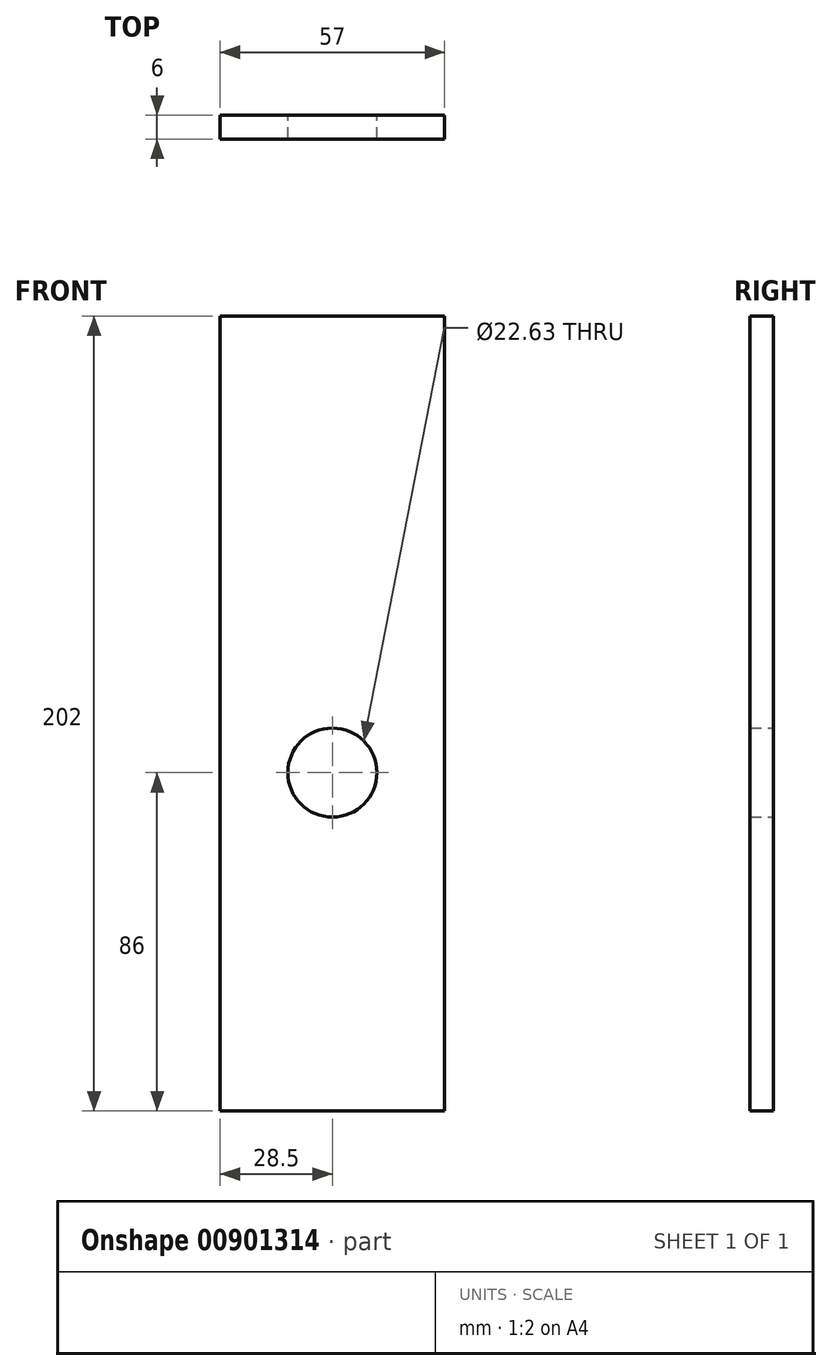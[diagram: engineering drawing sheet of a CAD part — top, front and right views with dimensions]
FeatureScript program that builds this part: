
annotation { "Feature Type Name" : "Feature", "Feature Type Description" : "" }
export const myFeature = defineFeature(function(context is Context, id is Id, definition is map)
    precondition{}
    {
        {
            var Q0;
            Q0=qCreatedBy(makeId("Front.planeOp"),FACE);
            var sketch = newSketch(context, id + "F0", { "sketchPlane" : qUnion([Q0])});
            skLineSegment(sketch, "E0.bottom", {"start": v(-28.5, -101) * mm, "end": v(28.5, -101) * mm});
            skLineSegment(sketch, "E0.top", {"start": v(-28.5, 101) * mm, "end": v(28.5, 101) * mm});
            skLineSegment(sketch, "E0.left", {"start": v(-28.5, -101) * mm, "end": v(-28.5, 101) * mm});
            skLineSegment(sketch, "E0.right", {"start": v(28.5, -101) * mm, "end": v(28.5, 101) * mm});
            skPoint(sketch, "E0.middle", {"position": v(0, 0) * mm});
            skLineSegment(sketch, "E1", {"start": v(-66.75, -7) * mm, "end": v(79.3, -7) * mm, "construction": true});
            skLineSegment(sketch, "E2.bottom", {"start": v(-8, -7) * mm, "end": v(8, -7) * mm});
            skLineSegment(sketch, "E2.top", {"start": v(-8, -23) * mm, "end": v(8, -23) * mm});
            skLineSegment(sketch, "E2.left", {"start": v(-8, -7) * mm, "end": v(-8, -23) * mm});
            skLineSegment(sketch, "E2.right", {"start": v(8, -7) * mm, "end": v(8, -23) * mm});
            skLineSegment(sketch, "E3", {"start": v(-8, -23) * mm, "end": v(8, -7) * mm, "construction": true});
            skLineSegment(sketch, "E4", {"start": v(-8, -7) * mm, "end": v(8, -23) * mm, "construction": true});
            skCircle(sketch, "E5", {"center": v(0, -15) * mm, "radius": 11.31 * mm});
            skSolve(sketch);
        }
        {
            var Q0;
            Q0 = qSketchRegion(id + "F0", true);
            extrude(context, id + "F1", {"entities" : qUnion([Q0]), "depth" : 6 * mm, "offsetDistance" : 25 * mm});
        }
    });
